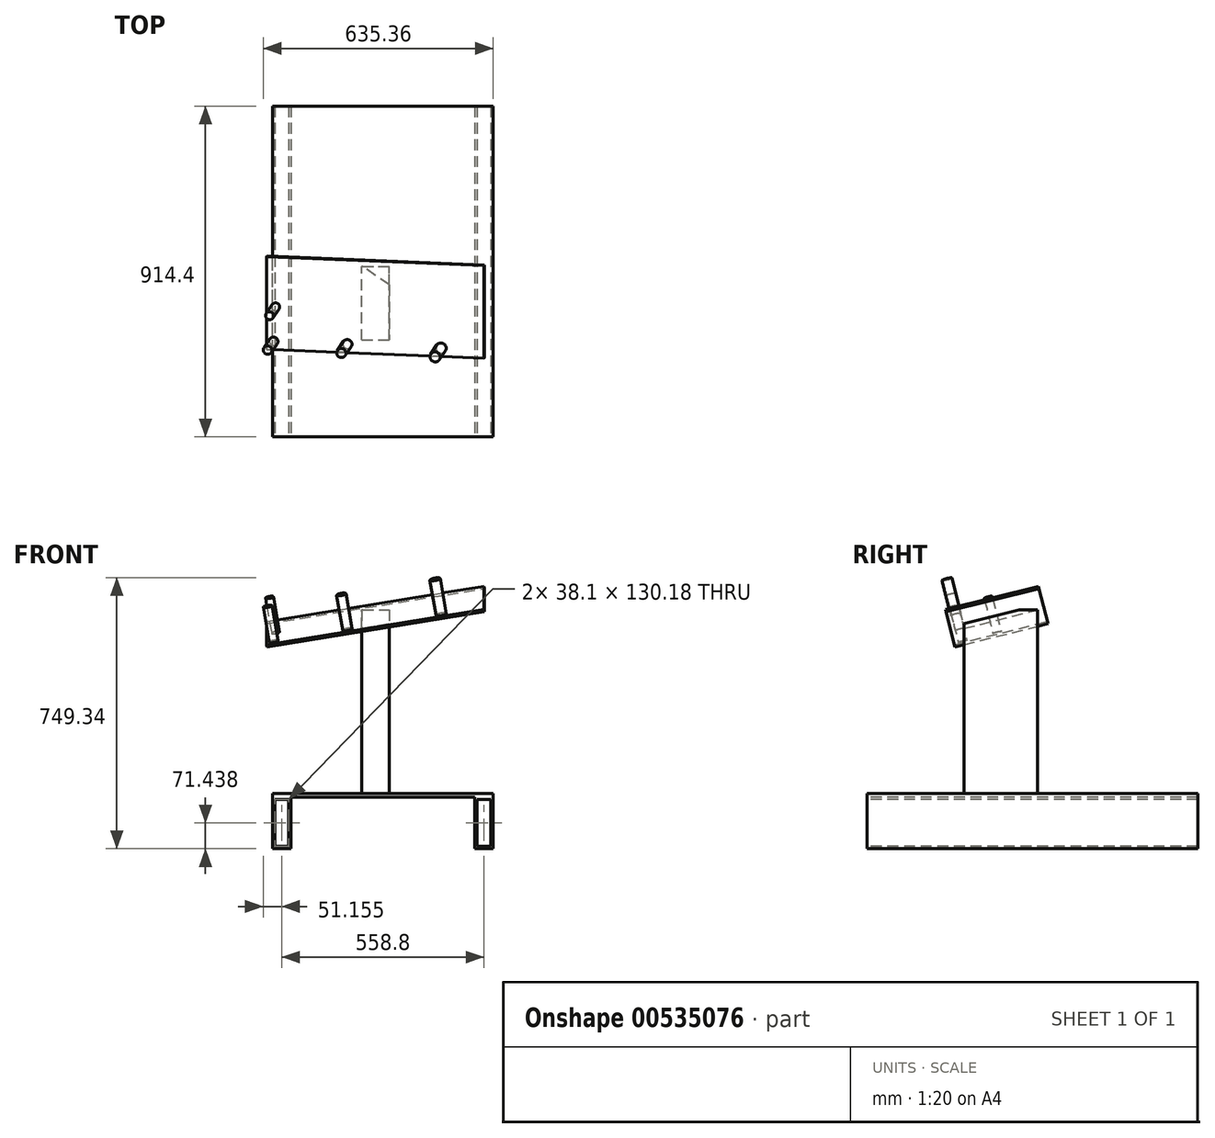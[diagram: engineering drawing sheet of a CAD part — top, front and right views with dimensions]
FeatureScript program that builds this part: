
annotation { "Feature Type Name" : "Feature", "Feature Type Description" : "" }
export const myFeature = defineFeature(function(context is Context, id is Id, definition is map)
    precondition{}
    {
        {
            var Q0;
            Q0=qCreatedBy(makeId("Top.planeOp"),FACE);
            var sketch = newSketch(context, id + "F0", { "sketchPlane" : qUnion([Q0])});
            skLineSegment(sketch, "E0.bottom", {"start": v(-284.57, -369.24) * mm, "end": v(325.03, -369.24) * mm});
            skLineSegment(sketch, "E0.top", {"start": v(-284.57, 545.16) * mm, "end": v(325.03, 545.16) * mm});
            skLineSegment(sketch, "E0.left", {"start": v(-284.57, -369.24) * mm, "end": v(-284.57, 545.16) * mm});
            skLineSegment(sketch, "E0.right", {"start": v(325.03, -369.24) * mm, "end": v(325.03, 545.16) * mm});
            skSolve(sketch);
        }
        {
            var Q0;
            Q0=makeQuery(id+"F0.imprint","IMPRINT",FACE,{"disambiguationData":[TD([[makeQuery(id+"F0.imprint","IMPRINT",EDGE,{"derivedFrom":sQuery(id+"F0.wireOp",EDGE,"E0.bottom")}),1.0]])]});
            extrude(context, id + "F1", {"entities" : qUnion([Q0]), "oppositeDirection" : true, "depth" : 152.4 * mm, "offsetDistance" : 25.4 * mm});
        }
        {
            var Q0;
            Q0=makeQuery(id+"F1.opExtrude","SWEPT_FACE",FACE,{"disambiguationData":[OSD([sQuery(id+"F0.wireOp",EDGE,"E0.bottom")])]});
            var sketch = newSketch(context, id + "F2", { "sketchPlane" : qUnion([Q0])});
            skLineSegment(sketch, "E1.bottom", {"start": v(-233.77, -152.4) * mm, "end": v(274.23, -152.4) * mm});
            skLineSegment(sketch, "E1.top", {"start": v(-233.77, -9.53) * mm, "end": v(274.23, -9.53) * mm});
            skLineSegment(sketch, "E1.left", {"start": v(-233.77, -152.4) * mm, "end": v(-233.77, -9.53) * mm});
            skLineSegment(sketch, "E1.right", {"start": v(274.23, -152.4) * mm, "end": v(274.23, -9.53) * mm});
            skSolve(sketch);
        }
        {
            var Q0;
            Q0 = qSketchRegion(id + "F2", true);
            extrude(context, id + "F3", {"entities" : qUnion([Q0]), "operationType" : NewBodyOperationType.REMOVE, "endBound" : BoundingType.THROUGH_ALL, "oppositeDirection" : true, "depth" : 25.4 * mm, "offsetDistance" : 25.4 * mm});
        }
        {
            var Q0;
            Q0=makeQuery(id+"F1.opExtrude","CAP_FACE",FACE,{"disambiguationData":[OSD([sQuery(id+"F0.wireOp",EDGE,"E0.bottom"),sQuery(id+"F0.wireOp",EDGE,"E0.top"),sQuery(id+"F0.wireOp",EDGE,"E0.left"),sQuery(id+"F0.wireOp",EDGE,"E0.right")])],"isStart":true});
            var sketch = newSketch(context, id + "F4", { "sketchPlane" : qUnion([Q0])});
            skLineSegment(sketch, "E2.bottom", {"start": v(-38.1, -101.6) * mm, "end": v(38.1, -101.6) * mm});
            skLineSegment(sketch, "E2.top", {"start": v(-38.1, 101.6) * mm, "end": v(38.1, 101.6) * mm});
            skLineSegment(sketch, "E2.left", {"start": v(-38.1, -101.6) * mm, "end": v(-38.1, 101.6) * mm});
            skLineSegment(sketch, "E2.right", {"start": v(38.1, -101.6) * mm, "end": v(38.1, 101.6) * mm});
            skSolve(sketch);
        }
        {
            var Q0;
            Q0=makeQuery(id+"F4.imprint","IMPRINT",FACE,{"disambiguationData":[TD([[makeQuery(id+"F4.imprint","IMPRINT",EDGE,{"derivedFrom":sQuery(id+"F4.wireOp",EDGE,"E2.bottom")}),1.0]])]});
            extrude(context, id + "F5", {"entities" : qUnion([Q0]), "operationType" : NewBodyOperationType.ADD, "depth" : 508 * mm, "offsetDistance" : 25.4 * mm});
        }
        {
            var Q0;
            Q0=makeQuery(id+"F5.opExtrude","SWEPT_FACE",FACE,{"disambiguationData":[OSD([sQuery(id+"F4.wireOp",EDGE,"E2.right")])]});
            var sketch = newSketch(context, id + "F6", { "sketchPlane" : qUnion([Q0])});
            skLineSegment(sketch, "E3", {"start": v(50.8, 508) * mm, "end": v(-101.6, 469.9) * mm});
            skSolve(sketch);
        }
        {
            var Q0;
            {var subQ0=sQuery(id+"F6.wireOp",EDGE,"E3");Q0=makeQuery(id+"F6.imprint","IMPRINT",FACE,{"disambiguationData":[TD([[makeQuery(id+"F6.imprint","IMPRINT",EDGE,{"derivedFrom":subQ0}),-1.0]])]});}
            extrude(context, id + "F7", {"entities" : qUnion([Q0]), "operationType" : NewBodyOperationType.REMOVE, "endBound" : BoundingType.THROUGH_ALL, "oppositeDirection" : true, "depth" : 25.4 * mm, "offsetDistance" : 25.4 * mm});
        }
        {
            var Q0;
            Q0=makeQuery(id+"F7.boolean.opBoolean","INTERSECT",EDGE,{"derivedFrom":[makeQuery(id+"F5.opExtrude","SWEPT_FACE",FACE,{"disambiguationData":[OSD([sQuery(id+"F4.wireOp",EDGE,"E2.left")])]}),makeQuery(id+"F7.opExtrude","SWEPT_FACE",FACE,{"disambiguationData":[OSD([sQuery(id+"F6.wireOp",EDGE,"E3")])]})]});
            chamfer(context, id + "F8", {"entities" : qUnion([Q0]), "chamferType" : ChamferType.TWO_OFFSETS, "width1" : 12.7 * mm, "oppositeDirection" : false, "width2" : 76.2 * mm, "tangentPropagation" : true});
        }
        {
            var Q0;
            Q0=makeQuery(id+"F8.opChamfer","BLEND_FACE",FACE,{"disambiguationData":[OSD([sQuery(id+"F4.wireOp",EDGE,"E2.left"),sQuery(id+"F6.wireOp",EDGE,"E3")])]});
            var sketch = newSketch(context, id + "F9", { "sketchPlane" : qUnion([Q0])});
            skLineSegment(sketch, "E4.bottom", {"start": v(-226.32, -24.11) * mm, "end": v(383.28, -24.11) * mm});
            skLineSegment(sketch, "E4.top", {"start": v(-226.32, 240.73) * mm, "end": v(383.28, 240.73) * mm});
            skLineSegment(sketch, "E4.left", {"start": v(-226.32, -24.11) * mm, "end": v(-226.32, 240.73) * mm});
            skLineSegment(sketch, "E4.right", {"start": v(383.28, -24.11) * mm, "end": v(383.28, 240.73) * mm});
            skSolve(sketch);
        }
        {
            var Q0;
            Q0 = qSketchRegion(id + "F9", true);
            extrude(context, id + "F10", {"entities" : qUnion([Q0]), "operationType" : NewBodyOperationType.ADD, "depth" : 6.35 * mm, "offsetDistance" : 25.4 * mm});
        }
        {
            var Q0;
            Q0=makeQuery(id+"F10.opExtrude","CAP_FACE",FACE,{"disambiguationData":[OSD([sQuery(id+"F9.wireOp",EDGE,"E4.bottom"),sQuery(id+"F9.wireOp",EDGE,"E4.top"),sQuery(id+"F9.wireOp",EDGE,"E4.left"),sQuery(id+"F9.wireOp",EDGE,"E4.right")])],"isStart":false});
            var sketch = newSketch(context, id + "F11", { "sketchPlane" : qUnion([Q0])});
            skCircle(sketch, "E5", {"center": v(-206.57, 0) * mm, "radius": 12.1 * mm});
            skCircle(sketch, "E6", {"center": v(-201, 98.41) * mm, "radius": 11.43 * mm});
            skCircle(sketch, "E7", {"center": v(0, 0.4) * mm, "radius": 13.05 * mm});
            skCircle(sketch, "E8", {"center": v(262.71, 0) * mm, "radius": 14.35 * mm});
            skSolve(sketch);
        }
        {
            var Q0;
            Q0 = qSketchRegion(id + "F11", true);
            extrude(context, id + "F12", {"entities" : qUnion([Q0]), "operationType" : NewBodyOperationType.ADD, "depth" : 101.6 * mm, "offsetDistance" : 25.4 * mm});
        }
        {
            var Q0;
            Q0 = qSketchRegion(id + "F11", true);
            extrude(context, id + "F13", {"entities" : qUnion([Q0]), "operationType" : NewBodyOperationType.ADD, "depth" : 25.4 * mm, "offsetDistance" : 25.4 * mm});
        }
        {
            var Q0;
            Q0=makeQuery(id+"F1.opExtrude","SWEPT_FACE",FACE,{"disambiguationData":[OSD([sQuery(id+"F0.wireOp",EDGE,"E0.bottom")])]});
            var sketch = newSketch(context, id + "F14", { "sketchPlane" : qUnion([Q0])});
            skLineSegment(sketch, "E9.bottom", {"start": v(-278.22, -146.05) * mm, "end": v(-240.12, -146.05) * mm});
            skLineSegment(sketch, "E9.top", {"start": v(-278.22, -15.88) * mm, "end": v(-240.12, -15.88) * mm});
            skLineSegment(sketch, "E9.left", {"start": v(-278.22, -146.05) * mm, "end": v(-278.22, -15.88) * mm});
            skLineSegment(sketch, "E9.right", {"start": v(-240.12, -146.05) * mm, "end": v(-240.12, -15.88) * mm});
            skLineSegment(sketch, "E10.bottom", {"start": v(318.68, -146.05) * mm, "end": v(280.58, -146.05) * mm});
            skLineSegment(sketch, "E10.top", {"start": v(318.68, -15.88) * mm, "end": v(280.58, -15.88) * mm});
            skLineSegment(sketch, "E10.left", {"start": v(318.68, -146.05) * mm, "end": v(318.68, -15.88) * mm});
            skLineSegment(sketch, "E10.right", {"start": v(280.58, -146.05) * mm, "end": v(280.58, -15.88) * mm});
            skSolve(sketch);
        }
        {
            var Q0;
            Q0 = qSketchRegion(id + "F14", true);
            extrude(context, id + "F15", {"entities" : qUnion([Q0]), "operationType" : NewBodyOperationType.REMOVE, "endBound" : BoundingType.THROUGH_ALL, "oppositeDirection" : true, "depth" : 25.4 * mm, "offsetDistance" : 25.4 * mm});
        }
    });
